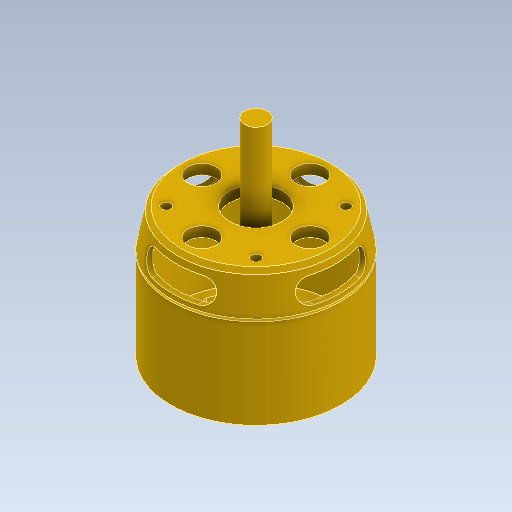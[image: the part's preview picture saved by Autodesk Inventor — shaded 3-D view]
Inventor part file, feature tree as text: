
AUTODESK INVENTOR PART (.ipt)
format: ipt  version: 2023 (Build 270158000, 158)  size: 348,160 bytes
history: native  units: in
note: dims shown in document units (in); Inventor stores cm internally (conversion verified against a paired STEP export)
features: extrude x4, sketch x4, pattern_circular x2, revolve x1, plane x1
ambient origin geometry x8: Origin, YZ Plane, XZ Plane, XY Plane, X Axis, Y Axis, Z Axis, Center Point
bodies: Solid1 (feature_tree)
feature tree (12):
  revolve  "Revolution1"  [1 undecoded]
  extrude  "Extrusion1"  Depth=0.5161in
  plane  "Work Plane1"
  extrude  "Extrusion2"  Depth=0.0787in
  sketch  "Sketch4"  dims[d6=45.0deg d7=0.3616in d8=0.0315in d9=1.2252in d10=0.1102in d11=0.1575in d12=3.2677in d13=1.0433in d14=0.0835in d16=0.0709in d17=0.1102in d18=0.3248in d19=0.6713in d20=90.0deg d21=0.3878in d22=0.128in d23=45.0deg d24=0.8661in d25=0.7382in d26=0.3937in d27=0.0in d28=1.1875in d29=0.315in d30=0.315in d31=0.2165in d32=0.6299in d33=0.3937in d34=0.0in d35=0.0906in d36=0.3937in d37=45.0deg d38=0.3937in d39=0.0in d40=1.5748in d41=360.0deg d43=0.9843in d44=2.0472in d46=0.3937in d47=0.0787in d48=0.3937in d49=0.0in d50=1.9685in d51=360.0deg]
  extrude  "Extrusion3"  Depth=0.3937in
  pattern_circular  "Circular Pattern1"  [2 undecoded]
  extrude  "Extrusion4"  Depth=0.3937in
  pattern_circular  "Circular Pattern2"  [2 undecoded]
  sketch  "Sketch1"  dims[d0=0.1378in d1=1.1614in]
  sketch  "Sketch2"  dims[d2=0.0709in d3=0.5161in]
  sketch  "Sketch3"  dims[d4=1.0573in d5=0.0787in]
note: 5 required parameter values undecoded (feature->parameter linkage not recoverable at this tier; creation-order binding heuristic only, values carry confidence <= 0.55)